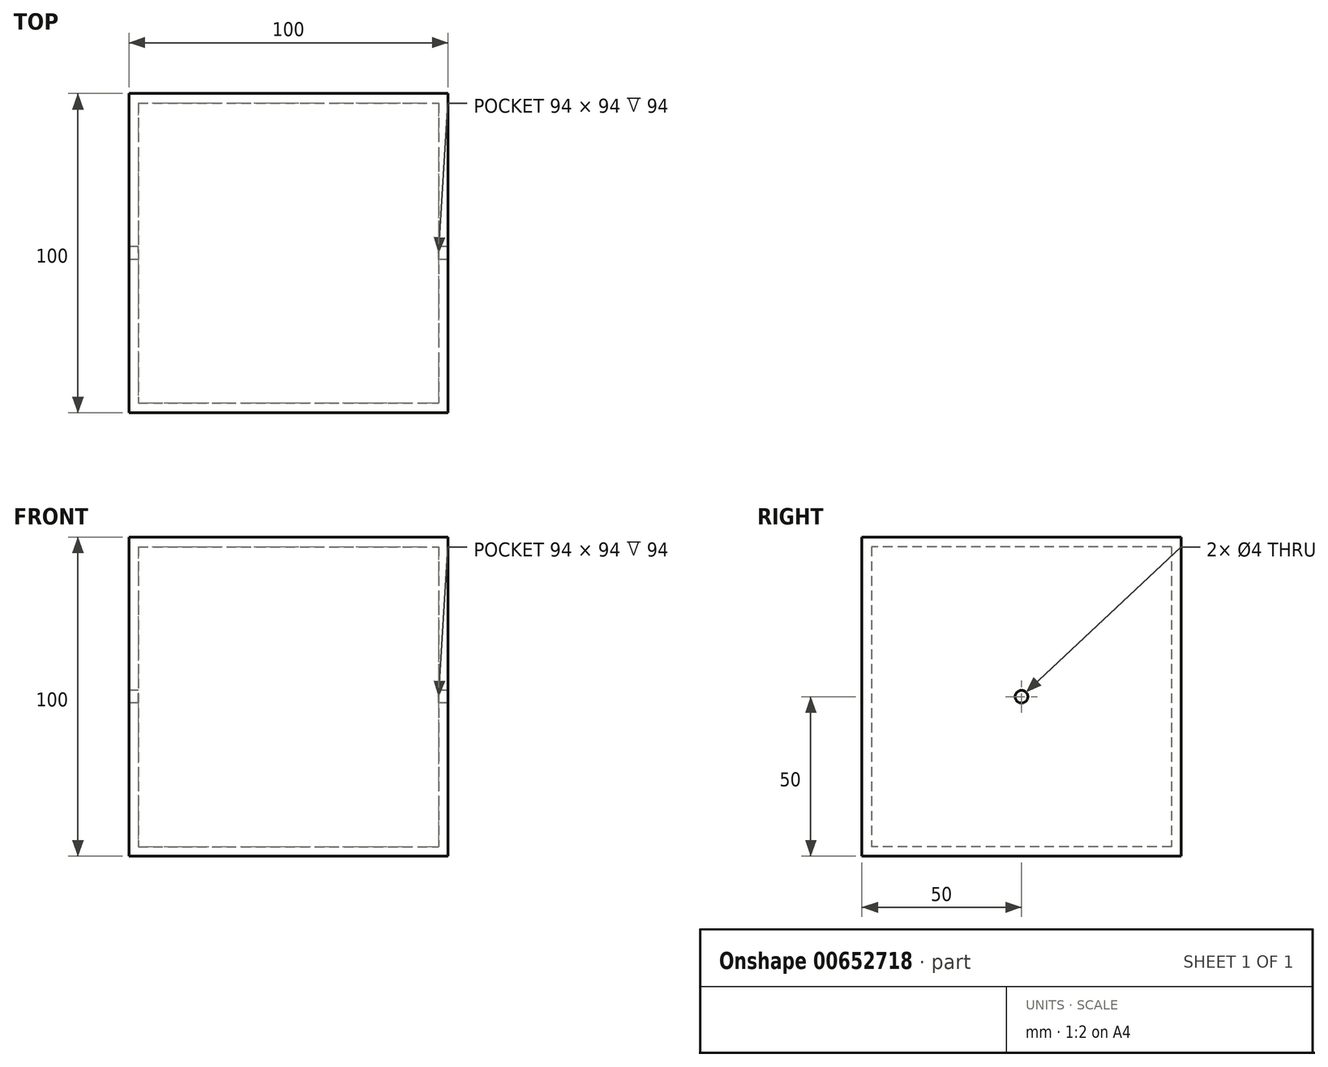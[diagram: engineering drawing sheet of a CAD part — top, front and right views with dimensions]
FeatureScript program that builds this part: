
annotation { "Feature Type Name" : "Feature", "Feature Type Description" : "" }
export const myFeature = defineFeature(function(context is Context, id is Id, definition is map)
    precondition{}
    {
        {
            var Q0;
            Q0=qCreatedBy(makeId("Top.planeOp"),FACE);
            var sketch = newSketch(context, id + "F0", { "sketchPlane" : qUnion([Q0])});
            skLineSegment(sketch, "E0.bottom", {"start": v(-50, 50) * mm, "end": v(50, 50) * mm});
            skLineSegment(sketch, "E0.top", {"start": v(-50, -50) * mm, "end": v(50, -50) * mm});
            skLineSegment(sketch, "E0.left", {"start": v(-50, 50) * mm, "end": v(-50, -50) * mm});
            skLineSegment(sketch, "E0.right", {"start": v(50, 50) * mm, "end": v(50, -50) * mm});
            skPoint(sketch, "E0.middle", {"position": v(0, 0) * mm});
            skSolve(sketch);
        }
        {
            var Q0;
            Q0 = qSketchRegion(id + "F0", true);
            var Q1;
            Q1 = qConstructionFilter(qBodyType(qCreatedBy(id + "F0" ,EDGE), BodyType.WIRE), ConstructionObject.NO);
            extrude(context, id + "F1", {"entities" : qUnion([Q0]), "surfaceEntities" : qUnion([Q1]), "depth" : 100 * mm, "offsetDistance" : 25 * mm});
        }
        {
            var Q0;
            Q0=makeQuery(id+"F1.opExtrude","CAP_FACE",FACE,{"disambiguationData":[OSD([sQuery(id+"F0.wireOp",EDGE,"E0.bottom"),sQuery(id+"F0.wireOp",EDGE,"E0.top"),sQuery(id+"F0.wireOp",EDGE,"E0.left"),sQuery(id+"F0.wireOp",EDGE,"E0.right")])],"isStart":false});
            var Q1;
            Q1=makeQuery(id+"F1.opExtrude","SWEPT_BODY",BODY,{"disambiguationData":[OSD([sQuery(id+"F0.wireOp",EDGE,"E0.bottom"),sQuery(id+"F0.wireOp",EDGE,"E0.top"),sQuery(id+"F0.wireOp",EDGE,"E0.left"),sQuery(id+"F0.wireOp",EDGE,"E0.right")])]});
            shell(context, id + "F2", {"isHollow" : true, "entities" : qUnion([Q0]), "parts" : qUnion([Q1]), "thickness" : 3 * mm});
        }
        {
            var Q0;
            Q0=makeQuery(id+"F1.opExtrude","SWEPT_FACE",FACE,{"disambiguationData":[OSD([sQuery(id+"F0.wireOp",EDGE,"E0.left")])]});
            var sketch = newSketch(context, id + "F3", { "sketchPlane" : qUnion([Q0])});
            skCircle(sketch, "E1", {"center": v(0, 50) * mm, "radius": 2 * mm});
            skSolve(sketch);
        }
        {
            var Q0;
            Q0 = qSketchRegion(id + "F3", true);
            extrude(context, id + "F4", {"entities" : qUnion([Q0]), "operationType" : NewBodyOperationType.REMOVE, "endBound" : BoundingType.THROUGH_ALL, "oppositeDirection" : true, "depth" : 25 * mm, "offsetDistance" : 25 * mm});
        }
        {
            var Q0;
            Q0=qCreatedBy(makeId("Right.planeOp"),FACE);
            var sketch = newSketch(context, id + "F5", { "sketchPlane" : qUnion([Q0])});
            skLineSegment(sketch, "E2", {"start": v(0, 0) * mm, "end": v(0, 135.86) * mm, "construction": true});
            skSolve(sketch);
        }
    });
